# Revit family: Direct-Storage-Vessel_Lochinvar_Ltd-LST-440_G_E_01
name_source: partatom
category: Mechanical Equipment
revit_build: Autodesk Revit 2013 (Build: 20120221_2030(x64)
units: mm (PartAtom-declared; Revit-internal decimal feet)

## types (1)
- Direct-Storage-Vessel_Lochinvar_Ltd-LST-440_G_E
    1e Maintenance (check-up) = 3 months after installation
    2nd Maintenance (general maintenance) = 12 months after installation
    Assembly Code = D3010
    BIM Content Developer = CAD & Company
    BIM Content Developer URL = http://www.cadcompany.nl
    CE-PIN = Lochinvar Limited
    Cold Water Connection R = 2"
    Description = Direct Storage Vessel
    Destination / Counrty = UK & Ireland
    Diameter (with insulation) = 600 mm
    Diameter (without insulation) = 550 mm
    Empty Weight = 350.00 kg
    Height (with insulation) = 2118 mm  [stored 6.94882 ft]
    Height (without insulation) = 2068 mm
    Height Cold Water Inlet = 135 mm
    Height Warm Water Outlet = 2058 mm
    Hot / Warm Water Connection R = 2"
    Insulation Thickness = 57 mm
    Length = 0 mm  [stored 0 ft]
    Maintenance Interval = 12 months
    Manufacturer Number = E 7110
E 7110
E 7110
    Max. Operating Pressure - tank = 1000000.0 Pa
    Max. Temperature - tank = 95 °C
    Model = LST 440 G E
    Operating Weight = 2230.00 kg
    Packaging Height = 2248 mm
    Packaging Length = 1426 mm
    Packaging Width = 1170 mm  [stored 3.83858 ft]
    Product Documentation Link = http://www.lochinvar.ltd.uk
    Product Instruction Link = http://www.lochinvar.ltd.uk
    Serial Number = 8717449269159
    Storage Capacity - tank = 1880 m³
    T&P Connection Rp = 1"
    Transport Weight = 440.00 kg
    Type of Packaging = Plastic and Wood
    URL = www.lochinvar.ltd.uk
    Warranty on Parts = 12 months
    Warranty on Tank = 36 months
    Width = 0 mm  [stored 0 ft]
    Workspace = 1100 mm

note: [stored X ft] marks values corroborated as IEEE doubles in the binary element streams (Revit-internal decimal feet)

## geometry (parser evidence)
native form markers: Sweep x11
no freeform markers — native parametric forms only
